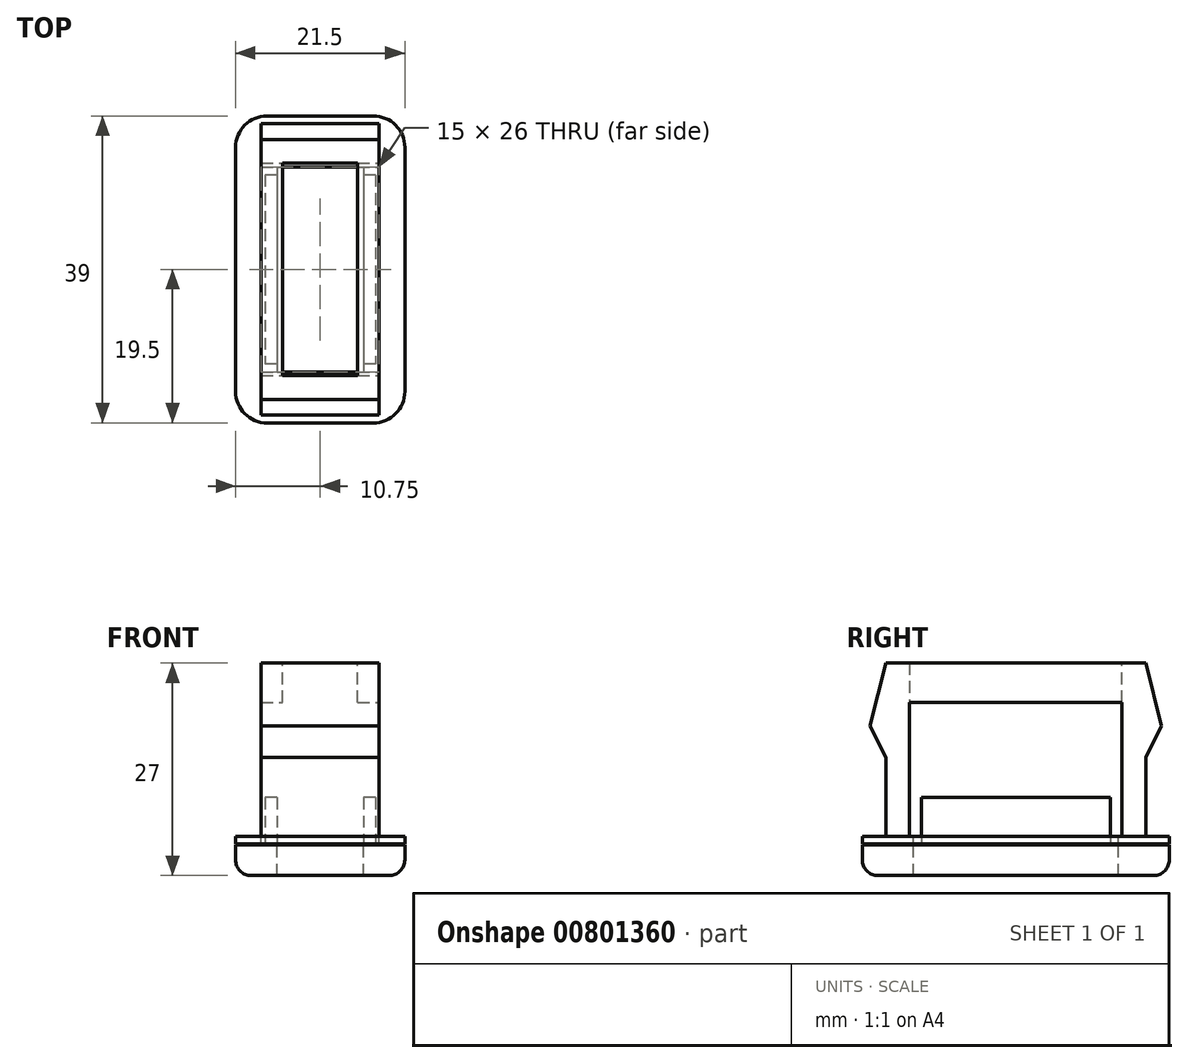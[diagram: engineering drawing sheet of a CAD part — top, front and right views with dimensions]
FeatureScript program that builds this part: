
annotation { "Feature Type Name" : "Feature", "Feature Type Description" : "" }
export const myFeature = defineFeature(function(context is Context, id is Id, definition is map)
    precondition{}
    {
        {
            var Q0;
            Q0=qCreatedBy(makeId("Top.planeOp"),FACE);
            var sketch = newSketch(context, id + "F0", { "sketchPlane" : qUnion([Q0])});
            skLineSegment(sketch, "E0.bottom", {"start": v(0, 0) * mm, "end": v(21.5, 0) * mm});
            skLineSegment(sketch, "E0.top", {"start": v(0, 39) * mm, "end": v(21.5, 39) * mm});
            skLineSegment(sketch, "E0.left", {"start": v(0, 0) * mm, "end": v(0, 39) * mm});
            skLineSegment(sketch, "E0.right", {"start": v(21.5, 0) * mm, "end": v(21.5, 39) * mm});
            skSolve(sketch);
        }
        {
            var Q0;
            Q0=makeQuery(id+"F0.imprint","IMPRINT",FACE,{"disambiguationData":[TD([[makeQuery(id+"F0.imprint","IMPRINT",EDGE,{"derivedFrom":sQuery(id+"F0.wireOp",EDGE,"E0.bottom")}),1.0]])]});
            extrude(context, id + "F1", {"entities" : qUnion([Q0]), "depth" : 5 * mm, "offsetDistance" : 25 * mm});
        }
        {
            var Q0;
            Q0=makeQuery(id+"F1.opExtrude","CAP_FACE",FACE,{"disambiguationData":[OSD([sQuery(id+"F0.wireOp",EDGE,"E0.bottom"),sQuery(id+"F0.wireOp",EDGE,"E0.top"),sQuery(id+"F0.wireOp",EDGE,"E0.left"),sQuery(id+"F0.wireOp",EDGE,"E0.right")])],"isStart":false});
            var sketch = newSketch(context, id + "F2", { "sketchPlane" : qUnion([Q0])});
            skLineSegment(sketch, "E1.bottom", {"start": v(3.25, 36) * mm, "end": v(18.25, 36) * mm});
            skLineSegment(sketch, "E1.top", {"start": v(3.25, 33) * mm, "end": v(18.25, 33) * mm});
            skLineSegment(sketch, "E1.left", {"start": v(3.25, 36) * mm, "end": v(3.25, 33) * mm});
            skLineSegment(sketch, "E1.right", {"start": v(18.25, 36) * mm, "end": v(18.25, 33) * mm});
            skLineSegment(sketch, "E2.bottom", {"start": v(3.25, 6) * mm, "end": v(18.25, 6) * mm});
            skLineSegment(sketch, "E2.top", {"start": v(3.25, 3) * mm, "end": v(18.25, 3) * mm});
            skLineSegment(sketch, "E2.left", {"start": v(3.25, 6) * mm, "end": v(3.25, 3) * mm});
            skLineSegment(sketch, "E2.right", {"start": v(18.25, 6) * mm, "end": v(18.25, 3) * mm});
            skSolve(sketch);
        }
        {
            var Q0;
            Q0=makeQuery(id+"F2.imprint","IMPRINT",FACE,{"disambiguationData":[TD([[makeQuery(id+"F2.imprint","IMPRINT",EDGE,{"derivedFrom":sQuery(id+"F2.wireOp",EDGE,"E1.bottom")}),-1.0]])]});
            var Q1;
            Q1=makeQuery(id+"F2.imprint","IMPRINT",FACE,{"disambiguationData":[TD([[makeQuery(id+"F2.imprint","IMPRINT",EDGE,{"derivedFrom":sQuery(id+"F2.wireOp",EDGE,"E2.bottom")}),-1.0]])]});
            extrude(context, id + "F3", {"entities" : qUnion([Q0, Q1]), "operationType" : NewBodyOperationType.ADD, "depth" : 22 * mm, "offsetDistance" : 25 * mm});
        }
        {
            var Q0;
            Q0=makeQuery(id+"F3.opExtrude","SWEPT_FACE",FACE,{"disambiguationData":[OSD([sQuery(id+"F2.wireOp",EDGE,"E2.left")])]});
            var sketch = newSketch(context, id + "F4", { "sketchPlane" : qUnion([Q0])});
            skLineSegment(sketch, "E3", {"start": v(-3, 27) * mm, "end": v(-1, 19) * mm});
            skLineSegment(sketch, "E4", {"start": v(-1, 19) * mm, "end": v(-3, 15) * mm});
            skLineSegment(sketch, "E5", {"start": v(-3, 15) * mm, "end": v(-3, 27) * mm});
            skLineSegment(sketch, "E6", {"start": v(-36, 27) * mm, "end": v(-36, 15) * mm});
            skLineSegment(sketch, "E7", {"start": v(-36, 15) * mm, "end": v(-38, 19) * mm});
            skLineSegment(sketch, "E8", {"start": v(-38, 19) * mm, "end": v(-36, 27) * mm});
            skSolve(sketch);
        }
        {
            var Q0;
            Q0=makeQuery(id+"F4.imprint","IMPRINT",FACE,{"disambiguationData":[TD([[makeQuery(id+"F4.imprint","IMPRINT",EDGE,{"derivedFrom":sQuery(id+"F4.wireOp",EDGE,"E6")}),-1.0]])]});
            var Q1;
            Q1=makeQuery(id+"F4.imprint","IMPRINT",FACE,{"disambiguationData":[TD([[makeQuery(id+"F4.imprint","IMPRINT",EDGE,{"derivedFrom":sQuery(id+"F4.wireOp",EDGE,"E3")}),-1.0]])]});
            extrude(context, id + "F5", {"entities" : qUnion([Q0, Q1]), "operationType" : NewBodyOperationType.ADD, "oppositeDirection" : true, "depth" : 15 * mm, "offsetDistance" : 25 * mm});
        }
        {
            var Q0;
            Q0=makeQuery(id+"F1.opExtrude","SWEPT_EDGE",EDGE,{"disambiguationData":[OSD([sQuery(id+"F0.wireOp",EDGE,"E0.top"),sQuery(id+"F0.wireOp",EDGE,"E0.left")])]});
            var Q1;
            Q1=makeQuery(id+"F1.opExtrude","SWEPT_EDGE",EDGE,{"disambiguationData":[OSD([sQuery(id+"F0.wireOp",EDGE,"E0.bottom"),sQuery(id+"F0.wireOp",EDGE,"E0.left")])]});
            var Q2;
            Q2=makeQuery(id+"F1.opExtrude","SWEPT_EDGE",EDGE,{"disambiguationData":[OSD([sQuery(id+"F0.wireOp",EDGE,"E0.bottom"),sQuery(id+"F0.wireOp",EDGE,"E0.right")])]});
            var Q3;
            Q3=makeQuery(id+"F1.opExtrude","SWEPT_EDGE",EDGE,{"disambiguationData":[OSD([sQuery(id+"F0.wireOp",EDGE,"E0.top"),sQuery(id+"F0.wireOp",EDGE,"E0.right")])]});
            fillet(context, id + "F6", {"entities" : qUnion([Q0, Q1, Q2, Q3]), "radius" : 4 * mm, "tangentPropagation" : true, "allowEdgeOverflow" : false});
        }
        {
            var Q0;
            Q0=makeQuery(id+"F1.opExtrude","CAP_FACE",FACE,{"disambiguationData":[OSD([sQuery(id+"F0.wireOp",EDGE,"E0.bottom"),sQuery(id+"F0.wireOp",EDGE,"E0.top"),sQuery(id+"F0.wireOp",EDGE,"E0.left"),sQuery(id+"F0.wireOp",EDGE,"E0.right")])],"isStart":true});
            fillet(context, id + "F7", {"entities" : qUnion([Q0]), "radius" : 2 * mm, "tangentPropagation" : true, "allowEdgeOverflow" : false});
        }
        {
            var Q0;
            Q0=makeQuery(id+"F1.opExtrude","CAP_FACE",FACE,{"disambiguationData":[OSD([sQuery(id+"F0.wireOp",EDGE,"E0.bottom"),sQuery(id+"F0.wireOp",EDGE,"E0.top"),sQuery(id+"F0.wireOp",EDGE,"E0.left"),sQuery(id+"F0.wireOp",EDGE,"E0.right")])],"isStart":false});
            var sketch = newSketch(context, id + "F8", { "sketchPlane" : qUnion([Q0])});
            skLineSegment(sketch, "E9.bottom", {"start": v(5.25, 32.5) * mm, "end": v(16.25, 32.5) * mm});
            skLineSegment(sketch, "E9.top", {"start": v(5.25, 6.5) * mm, "end": v(16.25, 6.5) * mm});
            skLineSegment(sketch, "E9.left", {"start": v(5.25, 32.5) * mm, "end": v(5.25, 6.5) * mm});
            skLineSegment(sketch, "E9.right", {"start": v(16.25, 32.5) * mm, "end": v(16.25, 6.5) * mm});
            skSolve(sketch);
        }
        {
            var Q0;
            Q0=makeQuery(id+"F8.imprint","IMPRINT",FACE,{"disambiguationData":[TD([[makeQuery(id+"F8.imprint","IMPRINT",EDGE,{"derivedFrom":sQuery(id+"F8.wireOp",EDGE,"E9.bottom")}),-1.0]])]});
            extrude(context, id + "F9", {"entities" : qUnion([Q0]), "operationType" : NewBodyOperationType.REMOVE, "oppositeDirection" : true, "depth" : 6 * mm, "offsetDistance" : 25 * mm});
        }
        {
            var Q0;
            Q0=makeQuery(id+"F1.opExtrude","SWEPT_FACE",FACE,{"disambiguationData":[OSD([sQuery(id+"F0.wireOp",EDGE,"E0.right")])]});
            var sketch = newSketch(context, id + "F10", { "sketchPlane" : qUnion([Q0])});
            skLineSegment(sketch, "E10.bottom", {"start": v(-1.17, 4) * mm, "end": v(48.83, 4) * mm});
            skLineSegment(sketch, "E10.top", {"start": v(-1.17, 3.9) * mm, "end": v(48.83, 3.9) * mm});
            skLineSegment(sketch, "E10.left", {"start": v(-1.17, 4) * mm, "end": v(-1.17, 3.9) * mm});
            skLineSegment(sketch, "E10.right", {"start": v(48.83, 4) * mm, "end": v(48.83, 3.9) * mm});
            skSolve(sketch);
        }
        {
            var Q0;
            {var subQ0=sQuery(id+"F10.wireOp",EDGE,"E10.bottom");var subQ1=sQuery(id+"F0.wireOp",EDGE,"E0.right");var subQ2=makeQuery(id+"F1.opExtrude","SWEPT_FACE",FACE,{"disambiguationData":[OSD([subQ1])]});var subQ3=makeQuery(id+"F6.opFillet","BLEND_EDGE",EDGE,{"blendedFrom":[makeQuery(id+"F1.opExtrude","SWEPT_EDGE",EDGE,{"disambiguationData":[OSD([sQuery(id+"F0.wireOp",EDGE,"E0.bottom"),subQ1])]}),subQ2],"blendedInto":[subQ2]});var subQ4=makeQuery(id+"F10.imprint","INTERSECT",VERTEX,{"derivedFrom":[subQ3,subQ0]});Q0=makeQuery(id+"F10.imprint","IMPRINT",FACE,{"disambiguationData":[TD([[makeQuery(id+"F10.imprint","IMPRINT",EDGE,{"disambiguationData":[TD([[subQ4,-1.0]])],"derivedFrom":subQ0}),-1.0]])]});}
            var Q1;
            {var subQ0=sQuery(id+"F10.wireOp",EDGE,"E10.left");Q1=makeQuery(id+"F10.imprint","IMPRINT",FACE,{"disambiguationData":[TD([[makeQuery(id+"F10.imprint","IMPRINT",EDGE,{"derivedFrom":subQ0}),1.0]])]});}
            var Q2;
            {var subQ0=sQuery(id+"F10.wireOp",EDGE,"E10.right");Q2=makeQuery(id+"F10.imprint","IMPRINT",FACE,{"disambiguationData":[TD([[makeQuery(id+"F10.imprint","IMPRINT",EDGE,{"derivedFrom":subQ0}),-1.0]])]});}
            extrude(context, id + "F11", {"entities" : qUnion([Q0, Q1, Q2]), "operationType" : NewBodyOperationType.REMOVE, "oppositeDirection" : true, "depth" : 40 * mm, "offsetDistance" : 25 * mm});
        }
        {
            var Q0;
            Q0=makeQuery(id+"F3.opExtrude","CAP_FACE",FACE,{"disambiguationData":[OSD([sQuery(id+"F2.wireOp",EDGE,"E1.bottom"),sQuery(id+"F2.wireOp",EDGE,"E1.top"),sQuery(id+"F2.wireOp",EDGE,"E1.left"),sQuery(id+"F2.wireOp",EDGE,"E1.right")])],"isStart":false});
            var sketch = newSketch(context, id + "F12", { "sketchPlane" : qUnion([Q0])});
            skLineSegment(sketch, "E11.bottom", {"start": v(3.25, 33) * mm, "end": v(6, 33) * mm});
            skLineSegment(sketch, "E11.top", {"start": v(3.25, 5.99) * mm, "end": v(6, 5.99) * mm});
            skLineSegment(sketch, "E11.left", {"start": v(3.25, 33) * mm, "end": v(3.25, 5.99) * mm});
            skLineSegment(sketch, "E11.right", {"start": v(6, 33) * mm, "end": v(6, 5.99) * mm});
            skLineSegment(sketch, "E12.bottom", {"start": v(18.25, 5.99) * mm, "end": v(15.5, 5.99) * mm});
            skLineSegment(sketch, "E12.top", {"start": v(18.25, 33) * mm, "end": v(15.5, 33) * mm});
            skLineSegment(sketch, "E12.left", {"start": v(18.25, 5.99) * mm, "end": v(18.25, 33) * mm});
            skLineSegment(sketch, "E12.right", {"start": v(15.5, 5.99) * mm, "end": v(15.5, 33) * mm});
            skSolve(sketch);
        }
        {
            var Q0;
            Q0=makeQuery(id+"F12.imprint","IMPRINT",FACE,{"disambiguationData":[TD([[makeQuery(id+"F12.imprint","IMPRINT",EDGE,{"derivedFrom":sQuery(id+"F12.wireOp",EDGE,"E12.bottom")}),-1.0]])]});
            var Q1;
            Q1=makeQuery(id+"F12.imprint","IMPRINT",FACE,{"disambiguationData":[TD([[makeQuery(id+"F12.imprint","IMPRINT",EDGE,{"derivedFrom":sQuery(id+"F12.wireOp",EDGE,"E11.bottom")}),-1.0]])]});
            extrude(context, id + "F13", {"entities" : qUnion([Q0, Q1]), "operationType" : NewBodyOperationType.ADD, "oppositeDirection" : true, "depth" : 5 * mm, "offsetDistance" : 25 * mm});
        }
        {
            var Q0;
            Q0=makeQuery(id+"F1.opExtrude","CAP_FACE",FACE,{"disambiguationData":[OSD([sQuery(id+"F0.wireOp",EDGE,"E0.bottom"),sQuery(id+"F0.wireOp",EDGE,"E0.top"),sQuery(id+"F0.wireOp",EDGE,"E0.left"),sQuery(id+"F0.wireOp",EDGE,"E0.right")])],"isStart":false});
            var sketch = newSketch(context, id + "F14", { "sketchPlane" : qUnion([Q0])});
            skLineSegment(sketch, "E13.bottom", {"start": v(16.25, 32.5) * mm, "end": v(18.25, 32.5) * mm});
            skLineSegment(sketch, "E13.top", {"start": v(16.25, 6.5) * mm, "end": v(18.25, 6.5) * mm});
            skLineSegment(sketch, "E13.left", {"start": v(16.25, 32.5) * mm, "end": v(16.25, 6.5) * mm});
            skLineSegment(sketch, "E13.right", {"start": v(18.25, 32.5) * mm, "end": v(18.25, 6.5) * mm});
            skLineSegment(sketch, "E14.bottom", {"start": v(5.25, 6.5) * mm, "end": v(3.25, 6.5) * mm});
            skLineSegment(sketch, "E14.top", {"start": v(5.25, 32.5) * mm, "end": v(3.25, 32.5) * mm});
            skLineSegment(sketch, "E14.left", {"start": v(5.25, 6.5) * mm, "end": v(5.25, 32.5) * mm});
            skLineSegment(sketch, "E14.right", {"start": v(3.25, 6.5) * mm, "end": v(3.25, 32.5) * mm});
            skSolve(sketch);
        }
        {
            var Q0;
            Q0=makeQuery(id+"F14.imprint","IMPRINT",FACE,{"disambiguationData":[TD([[makeQuery(id+"F14.imprint","IMPRINT",EDGE,{"derivedFrom":sQuery(id+"F14.wireOp",EDGE,"E13.bottom")}),-1.0]])]});
            var Q1;
            Q1=makeQuery(id+"F14.imprint","IMPRINT",FACE,{"disambiguationData":[TD([[makeQuery(id+"F14.imprint","IMPRINT",EDGE,{"derivedFrom":sQuery(id+"F14.wireOp",EDGE,"E14.bottom")}),-1.0]])]});
            extrude(context, id + "F15", {"entities" : qUnion([Q0, Q1]), "operationType" : NewBodyOperationType.REMOVE, "oppositeDirection" : true, "depth" : 1 * mm, "offsetDistance" : 25 * mm});
        }
        {
            var Q0;
            Q0=makeQuery(id+"F11.boolean.opBoolean","COPY",FACE,{"derivedFrom":makeQuery(id+"F11.opExtrude","SWEPT_FACE",FACE,{"disambiguationData":[OSD([sQuery(id+"F10.wireOp",EDGE,"E10.top")])]})});
            var sketch = newSketch(context, id + "F16", { "sketchPlane" : qUnion([Q0])});
            skLineSegment(sketch, "E15.bottom", {"start": v(17.75, 31.5) * mm, "end": v(16.25, 31.5) * mm});
            skLineSegment(sketch, "E15.top", {"start": v(17.75, 7.5) * mm, "end": v(16.25, 7.5) * mm});
            skLineSegment(sketch, "E15.left", {"start": v(17.75, 31.5) * mm, "end": v(17.75, 7.5) * mm});
            skLineSegment(sketch, "E15.right", {"start": v(16.25, 31.5) * mm, "end": v(16.25, 7.5) * mm});
            skLineSegment(sketch, "E16.bottom", {"start": v(5.25, 31.5) * mm, "end": v(3.75, 31.5) * mm});
            skLineSegment(sketch, "E16.top", {"start": v(5.25, 7.5) * mm, "end": v(3.75, 7.5) * mm});
            skLineSegment(sketch, "E16.left", {"start": v(5.25, 31.5) * mm, "end": v(5.25, 7.5) * mm});
            skLineSegment(sketch, "E16.right", {"start": v(3.75, 31.5) * mm, "end": v(3.75, 7.5) * mm});
            skSolve(sketch);
        }
        {
            var Q0;
            Q0=makeQuery(id+"F16.imprint","IMPRINT",FACE,{"disambiguationData":[TD([[makeQuery(id+"F16.imprint","IMPRINT",EDGE,{"derivedFrom":sQuery(id+"F16.wireOp",EDGE,"E15.bottom")}),1.0]])]});
            var Q1;
            Q1=makeQuery(id+"F16.imprint","IMPRINT",FACE,{"disambiguationData":[TD([[makeQuery(id+"F16.imprint","IMPRINT",EDGE,{"derivedFrom":sQuery(id+"F16.wireOp",EDGE,"E16.bottom")}),1.0]])]});
            extrude(context, id + "F17", {"entities" : qUnion([Q0, Q1]), "operationType" : NewBodyOperationType.ADD, "depth" : 6 * mm, "offsetDistance" : 25 * mm});
        }
    });
